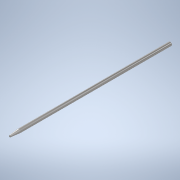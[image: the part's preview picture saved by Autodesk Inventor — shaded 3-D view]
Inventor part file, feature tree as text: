
AUTODESK INVENTOR PART (.ipt)
format: ipt  version: 2021 (Build 250183000, 183)  size: 97,280 bytes
history: native  units: mm
features: other x1, extrude x1, chamfer x1, sketch x1
ambient origin geometry x8: Origin, YZ Plane, XZ Plane, XY Plane, X Axis, Y Axis, Z Axis, Center Point
bodies: Body1 (feature_tree)
feature tree (4):
  other  "Bryła1"
  extrude  "Wyciągnięcie proste1"  Depth=4.0mm
  chamfer  "Faza1"  Distance=180.0mm
  sketch  "Szkic1"
